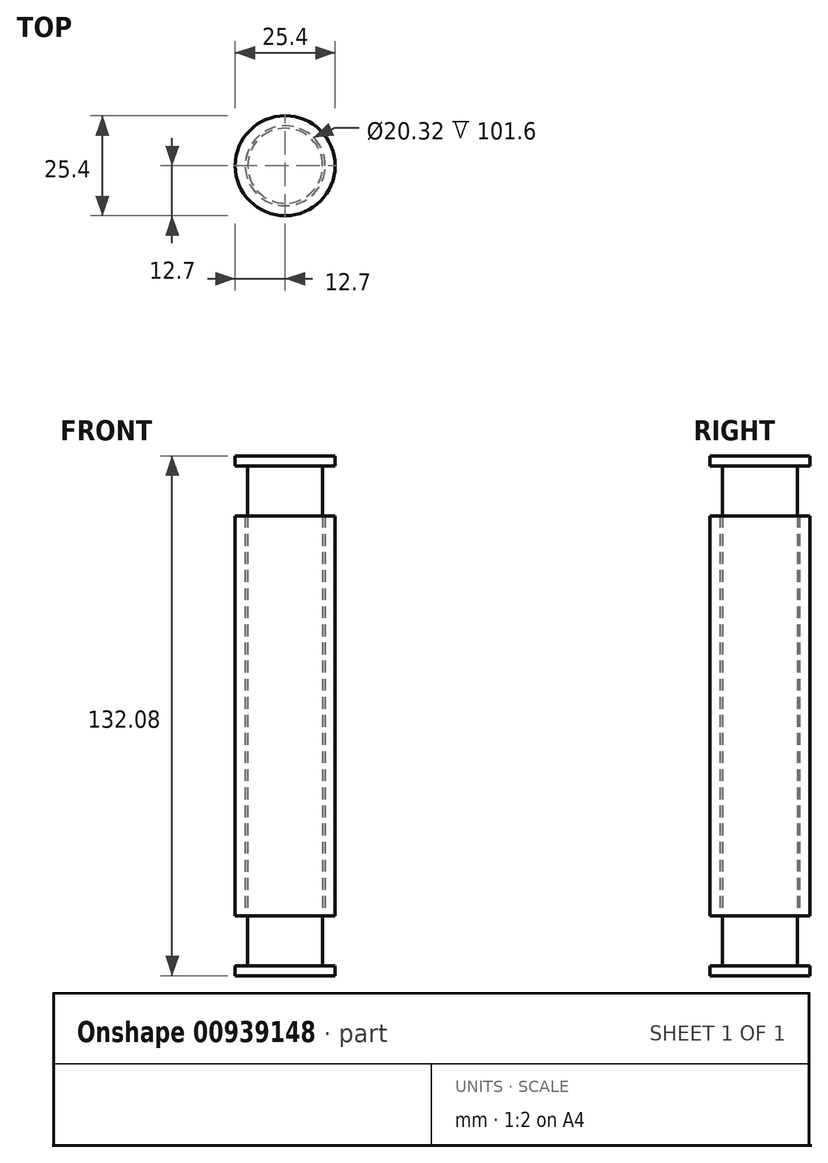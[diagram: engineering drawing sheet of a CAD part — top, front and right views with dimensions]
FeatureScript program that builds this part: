
annotation { "Feature Type Name" : "Feature", "Feature Type Description" : "" }
export const myFeature = defineFeature(function(context is Context, id is Id, definition is map)
    precondition{}
    {
        {
            var Q0;
            Q0=qCreatedBy(makeId("Front.planeOp"),FACE);
            var sketch = newSketch(context, id + "F0", { "sketchPlane" : qUnion([Q0])});
            skLineSegment(sketch, "E0.bottom", {"start": v(0, 0) * mm, "end": v(-9.52, 0) * mm});
            skLineSegment(sketch, "E0.top", {"start": v(0, 63.5) * mm, "end": v(-9.53, 63.5) * mm});
            skLineSegment(sketch, "E0.left", {"start": v(0, 0) * mm, "end": v(0, 63.5) * mm});
            skLineSegment(sketch, "E0.right", {"start": v(-9.52, 0) * mm, "end": v(-9.53, 63.5) * mm});
            skLineSegment(sketch, "E1.top", {"start": v(0, -63.5) * mm, "end": v(-9.52, -63.5) * mm});
            skLineSegment(sketch, "E1.left", {"start": v(0, 0) * mm, "end": v(0, -63.5) * mm});
            skLineSegment(sketch, "E1.right", {"start": v(-9.52, 0) * mm, "end": v(-9.52, -63.5) * mm});
            skLineSegment(sketch, "E2.bottom", {"start": v(-10.16, 0) * mm, "end": v(-12.7, 0) * mm});
            skLineSegment(sketch, "E2.top", {"start": v(-10.16, 50.8) * mm, "end": v(-12.7, 50.8) * mm});
            skLineSegment(sketch, "E2.left", {"start": v(-12.7, 0) * mm, "end": v(-12.7, 50.8) * mm});
            skLineSegment(sketch, "E2.right", {"start": v(-10.16, 0) * mm, "end": v(-10.16, 50.8) * mm});
            skLineSegment(sketch, "E3.top", {"start": v(-10.16, -50.8) * mm, "end": v(-12.7, -50.8) * mm});
            skLineSegment(sketch, "E3.left", {"start": v(-12.7, 0) * mm, "end": v(-12.7, -50.8) * mm});
            skLineSegment(sketch, "E3.right", {"start": v(-10.16, 0) * mm, "end": v(-10.16, -50.8) * mm});
            skPoint(sketch, "E4.endSnap0", {"position": v(0, -31.75) * mm});
            skLineSegment(sketch, "E5", {"start": v(-12.7, -31.69) * mm, "end": v(0, -31.75) * mm});
            skLineSegment(sketch, "E6.bottom", {"start": v(0, -63.5) * mm, "end": v(-12.7, -63.5) * mm});
            skLineSegment(sketch, "E6.top", {"start": v(0, -66.04) * mm, "end": v(-12.7, -66.04) * mm});
            skLineSegment(sketch, "E6.left", {"start": v(0, -63.5) * mm, "end": v(0, -66.04) * mm});
            skLineSegment(sketch, "E6.right", {"start": v(-12.7, -63.5) * mm, "end": v(-12.7, -66.04) * mm});
            skLineSegment(sketch, "E7.bottom", {"start": v(0, 63.5) * mm, "end": v(-12.7, 63.5) * mm});
            skLineSegment(sketch, "E7.top", {"start": v(0, 66.04) * mm, "end": v(-12.7, 66.04) * mm});
            skLineSegment(sketch, "E7.left", {"start": v(0, 63.5) * mm, "end": v(0, 66.04) * mm});
            skLineSegment(sketch, "E7.right", {"start": v(-12.7, 63.5) * mm, "end": v(-12.7, 66.04) * mm});
            skSolve(sketch);
        }
        {
            var Q0;
            {var subQ0=sQuery(id+"F0.wireOp",EDGE,"E0.left");Q0=makeQuery(id+"F0.imprint","IMPRINT",FACE,{"disambiguationData":[TD([[makeQuery(id+"F0.imprint","IMPRINT",EDGE,{"derivedFrom":subQ0}),1.0]])]});}
            var Q1;
            {var subQ0=sQuery(id+"F0.wireOp",EDGE,"E0.bottom");Q1=makeQuery(id+"F0.imprint","IMPRINT",FACE,{"disambiguationData":[TD([[makeQuery(id+"F0.imprint","IMPRINT",EDGE,{"derivedFrom":subQ0}),1.0]])]});}
            var Q2;
            {var subQ0=sQuery(id+"F0.wireOp",EDGE,"E6.bottom");var subQ5=sQuery(id+"F0.wireOp",EDGE,"E1.right");var subQ6=makeQuery(id+"F0.imprint","INTERSECT",VERTEX,{"derivedFrom":[subQ5,subQ0]});Q2=makeQuery(id+"F0.imprint","IMPRINT",FACE,{"disambiguationData":[TD([[makeQuery(id+"F0.imprint","IMPRINT",EDGE,{"disambiguationData":[TD([[subQ6,1.0]])],"derivedFrom":subQ5}),1.0]])]});}
            var Q3;
            Q3=sQuery(id+"F0.wireOp",EDGE,"E0.left");
            revolve(context, id + "F1", {"surfaceOperationType" : NewSurfaceOperationType.NEW, "entities" : qUnion([Q0, Q1, Q2]), "axis" : qUnion([Q3]), "revolveType" : RevolveType.FULL});
        }
        {
            var Q0;
            Q0=makeQuery(id+"F0.imprint","IMPRINT",FACE,{"disambiguationData":[TD([[makeQuery(id+"F0.imprint","IMPRINT",EDGE,{"derivedFrom":sQuery(id+"F0.wireOp",EDGE,"E7.top")}),1.0]])]});
            var Q1;
            Q1=sQuery(id+"F0.wireOp",EDGE,"E7.left");
            revolve(context, id + "F2", {"operationType" : NewBodyOperationType.ADD, "surfaceOperationType" : NewSurfaceOperationType.NEW, "entities" : qUnion([Q0]), "axis" : qUnion([Q1]), "revolveType" : RevolveType.FULL});
        }
        {
            var Q0;
            Q0=makeQuery(id+"F0.imprint","IMPRINT",FACE,{"disambiguationData":[TD([[makeQuery(id+"F0.imprint","IMPRINT",EDGE,{"derivedFrom":sQuery(id+"F0.wireOp",EDGE,"E6.top")}),-1.0]])]});
            var Q1;
            Q1=sQuery(id+"F0.wireOp",EDGE,"E6.left");
            revolve(context, id + "F3", {"operationType" : NewBodyOperationType.ADD, "surfaceOperationType" : NewSurfaceOperationType.NEW, "entities" : qUnion([Q0]), "axis" : qUnion([Q1]), "revolveType" : RevolveType.FULL});
        }
        {
            var Q0;
            Q0=makeQuery(id+"F0.imprint","IMPRINT",FACE,{"disambiguationData":[TD([[makeQuery(id+"F0.imprint","IMPRINT",EDGE,{"derivedFrom":sQuery(id+"F0.wireOp",EDGE,"E2.top")}),1.0]])]});
            var Q1;
            {var subQ0=sQuery(id+"F0.wireOp",EDGE,"E2.bottom");Q1=makeQuery(id+"F0.imprint","IMPRINT",FACE,{"disambiguationData":[TD([[makeQuery(id+"F0.imprint","IMPRINT",EDGE,{"derivedFrom":subQ0}),1.0]])]});}
            var Q2;
            {var subQ0=sQuery(id+"F0.wireOp",EDGE,"E3.top");Q2=makeQuery(id+"F0.imprint","IMPRINT",FACE,{"disambiguationData":[TD([[makeQuery(id+"F0.imprint","IMPRINT",EDGE,{"derivedFrom":subQ0}),-1.0]])]});}
            var Q3;
            Q3=sQuery(id+"F0.wireOp",EDGE,"E0.left");
            revolve(context, id + "F4", {"surfaceOperationType" : NewSurfaceOperationType.NEW, "entities" : qUnion([Q0, Q1, Q2]), "axis" : qUnion([Q3]), "revolveType" : RevolveType.FULL});
        }
    });
